# Revit family: FU_Chair_Sandler_Hellen Plus SE01
name_source: partatom
category: Furniture
units: mm (PartAtom-declared; Revit-internal decimal feet)

## family parameters
Always vertical = Yes
Cut with Voids When Loaded = No
OmniClass Number = 23.40.20.00
OmniClass Title = General Furniture and Specialties
Room Calculation Point = No
Shared = No
Work Plane-Based = No

## types (1)
- Hellen Plus SE01
    Default Elevation = 0 mm  [stored 0 ft]
    Depth = 550 mm
    Description = Chair on a solid beech wood frame with curved backrest. Stackable up to five chairs.
    Frame = Wood - Beech - Wenge - V
    Height = 825 mm  [stored 2.70669 ft]
    Manufacturer = Sandler
    Model = Hellen Plus SE01
    URL = https://www.sandlerseating.com
    Width = 550 mm

note: [stored X ft] marks values corroborated as IEEE doubles in the binary element streams (Revit-internal decimal feet)

## geometry (parser evidence)
native form markers: Sweep x7
no freeform markers — native parametric forms only
